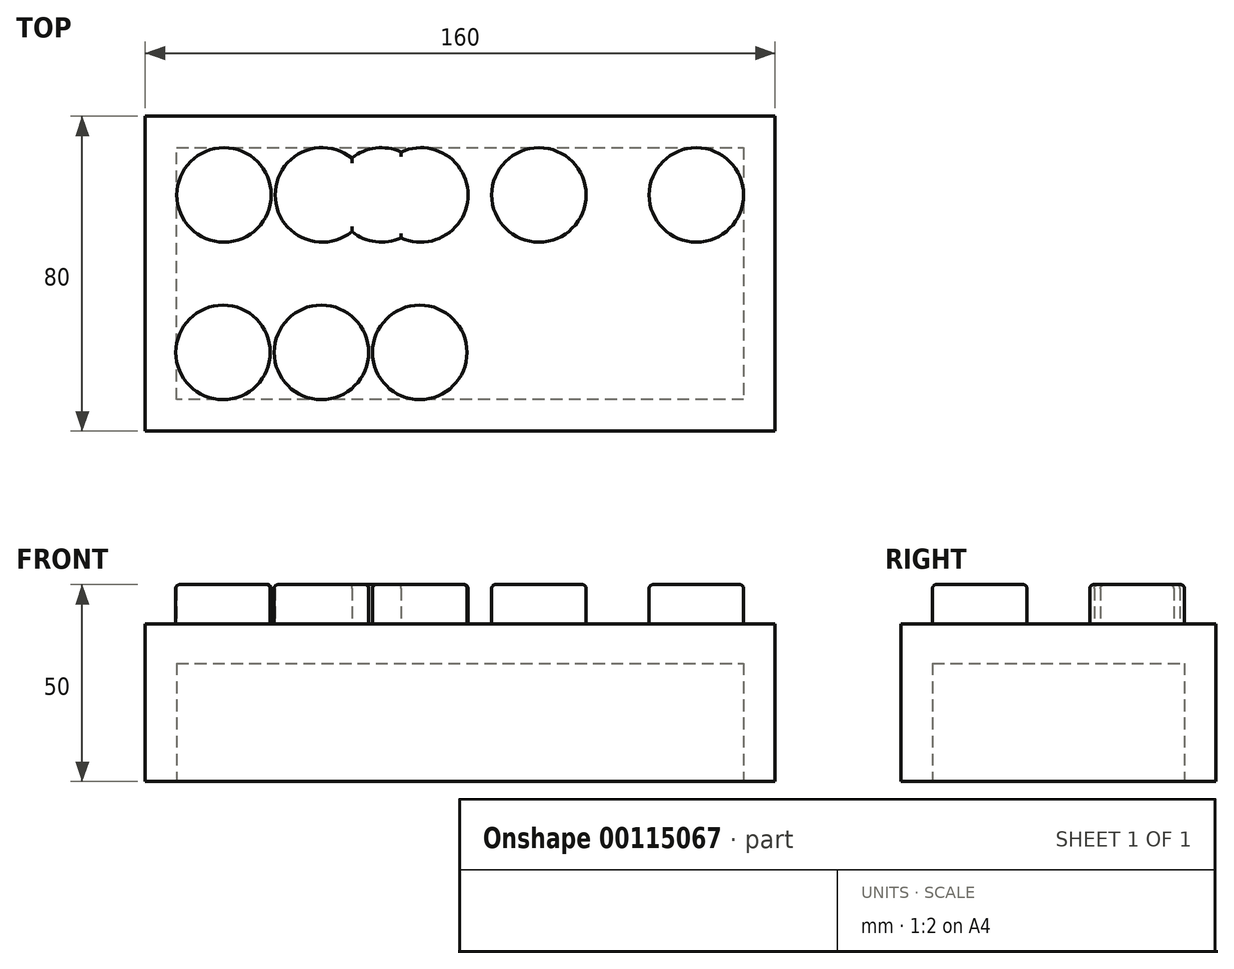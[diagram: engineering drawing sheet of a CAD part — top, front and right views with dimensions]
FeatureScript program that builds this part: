
annotation { "Feature Type Name" : "Feature", "Feature Type Description" : "" }
export const myFeature = defineFeature(function(context is Context, id is Id, definition is map)
    precondition{}
    {
        {
            var Q0;
            Q0=qCreatedBy(makeId("Top.planeOp"),FACE);
            var sketch = newSketch(context, id + "F0", { "sketchPlane" : qUnion([Q0])});
            skLineSegment(sketch, "E0.bottom", {"start": v(-79.83, 49.22) * mm, "end": v(80.17, 49.22) * mm});
            skLineSegment(sketch, "E0.top", {"start": v(-79.83, -30.78) * mm, "end": v(80.17, -30.78) * mm});
            skLineSegment(sketch, "E0.left", {"start": v(-79.83, 49.22) * mm, "end": v(-79.83, -30.78) * mm});
            skLineSegment(sketch, "E0.right", {"start": v(80.17, 49.22) * mm, "end": v(80.17, -30.78) * mm});
            skSolve(sketch);
        }
        {
            var Q0;
            Q0 = qSketchRegion(id + "F0", true);
            extrude(context, id + "F1", {"entities" : qUnion([Q0]), "depth" : 40 * mm});
        }
        {
            var Q0;
            Q0=makeQuery(id+"F1.opExtrude","CAP_FACE",FACE,{"disambiguationData":[OSD([sQuery(id+"F0.wireOp",EDGE,"E0.bottom"),sQuery(id+"F0.wireOp",EDGE,"E0.top"),sQuery(id+"F0.wireOp",EDGE,"E0.left"),sQuery(id+"F0.wireOp",EDGE,"E0.right")])],"isStart":true});
            var sketch = newSketch(context, id + "F2", { "sketchPlane" : qUnion([Q0])});
            skLineSegment(sketch, "E1.0", {"start": v(-71.83, -41.22) * mm, "end": v(72.17, -41.22) * mm});
            skLineSegment(sketch, "E1.1", {"start": v(-71.83, 22.78) * mm, "end": v(-71.83, -41.22) * mm});
            skLineSegment(sketch, "E1.2", {"start": v(72.17, 22.78) * mm, "end": v(-71.83, 22.78) * mm});
            skLineSegment(sketch, "E1.3", {"start": v(72.17, -41.22) * mm, "end": v(72.17, 22.78) * mm});
            skSolve(sketch);
        }
        {
            var Q0;
            Q0=makeQuery(id+"F2.imprint","IMPRINT",FACE,{"disambiguationData":[TD([[makeQuery(id+"F2.imprint","IMPRINT",EDGE,{"derivedFrom":sQuery(id+"F2.wireOp",EDGE,"E1.0")}),1.0]])]});
            extrude(context, id + "F3", {"entities" : qUnion([Q0]), "operationType" : NewBodyOperationType.REMOVE, "oppositeDirection" : true, "depth" : 30 * mm});
        }
        {
            var Q0;
            Q0=makeQuery(id+"F1.opExtrude","CAP_FACE",FACE,{"disambiguationData":[OSD([sQuery(id+"F0.wireOp",EDGE,"E0.bottom"),sQuery(id+"F0.wireOp",EDGE,"E0.top"),sQuery(id+"F0.wireOp",EDGE,"E0.left"),sQuery(id+"F0.wireOp",EDGE,"E0.right")])],"isStart":false});
            var sketch = newSketch(context, id + "F4", { "sketchPlane" : qUnion([Q0])});
            skCircle(sketch, "E2", {"center": v(-59.83, 29.22) * mm, "radius": 12 * mm});
            skCircle(sketch, "E3.1.0.0", {"center": v(-19.83, 29.22) * mm, "radius": 12 * mm});
            skCircle(sketch, "E3.2.0.0", {"center": v(20.17, 29.22) * mm, "radius": 12 * mm});
            skCircle(sketch, "E3.3.0.0", {"center": v(60.17, 29.22) * mm, "radius": 12 * mm});
            skLineSegment(sketch, "E3.direction1", {"start": v(-59.83, 29.22) * mm, "end": v(-19.83, 29.22) * mm, "construction": true});
            skCircle(sketch, "E4.0.1.0", {"center": v(-60.09, -10.78) * mm, "radius": 12 * mm});
            skCircle(sketch, "E4.1.0.0", {"center": v(-34.83, 29.22) * mm, "radius": 12 * mm});
            skCircle(sketch, "E4.1.1.0", {"center": v(-35.09, -10.78) * mm, "radius": 12 * mm});
            skCircle(sketch, "E4.2.0.0", {"center": v(-9.83, 29.22) * mm, "radius": 12 * mm});
            skCircle(sketch, "E4.2.1.0", {"center": v(-10.09, -10.78) * mm, "radius": 12 * mm});
            skLineSegment(sketch, "E4.direction1", {"start": v(-59.83, 29.22) * mm, "end": v(-34.83, 29.22) * mm, "construction": true});
            skLineSegment(sketch, "E4.direction2", {"start": v(-59.83, 29.22) * mm, "end": v(-60.09, -10.78) * mm, "construction": true});
            skSolve(sketch);
        }
        {
            var Q0;
            Q0 = qSketchRegion(id + "F4", true);
            extrude(context, id + "F5", {"entities" : qUnion([Q0]), "operationType" : NewBodyOperationType.ADD, "depth" : 10 * mm});
        }
        {
            var Q0;
            Q0=makeQuery(id+"F5.opExtrude","CAP_FACE",FACE,{"disambiguationData":[OSD([sQuery(id+"F4.wireOp",EDGE,"E3.2.0.0")])],"isStart":false});
            var Q1;
            Q1=makeQuery(id+"F5.opExtrude","CAP_FACE",FACE,{"disambiguationData":[OSD([sQuery(id+"F4.wireOp",EDGE,"E3.3.0.0")])],"isStart":false});
            var Q2;
            Q2=makeQuery(id+"F5.opExtrude","CAP_FACE",FACE,{"disambiguationData":[OSD([sQuery(id+"F4.wireOp",EDGE,"E3.1.0.0"),sQuery(id+"F4.wireOp",EDGE,"E4.1.0.0"),sQuery(id+"F4.wireOp",EDGE,"E4.2.0.0")])],"isStart":false});
            var Q3;
            Q3=makeQuery(id+"F5.opExtrude","CAP_FACE",FACE,{"disambiguationData":[OSD([sQuery(id+"F4.wireOp",EDGE,"E2")])],"isStart":false});
            var Q4;
            Q4=makeQuery(id+"F5.opExtrude","CAP_FACE",FACE,{"disambiguationData":[OSD([sQuery(id+"F4.wireOp",EDGE,"E4.0.1.0")])],"isStart":false});
            var Q5;
            Q5=makeQuery(id+"F5.opExtrude","CAP_FACE",FACE,{"disambiguationData":[OSD([sQuery(id+"F4.wireOp",EDGE,"E4.1.1.0")])],"isStart":false});
            var Q6;
            Q6=makeQuery(id+"F5.opExtrude","CAP_FACE",FACE,{"disambiguationData":[OSD([sQuery(id+"F4.wireOp",EDGE,"E4.2.1.0")])],"isStart":false});
            fillet(context, id + "F6", {"entities" : qUnion([Q0, Q1, Q2, Q3, Q4, Q5, Q6]), "radius" : 1 * mm, "tangentPropagation" : true, "allowEdgeOverflow" : false});
        }
    });
